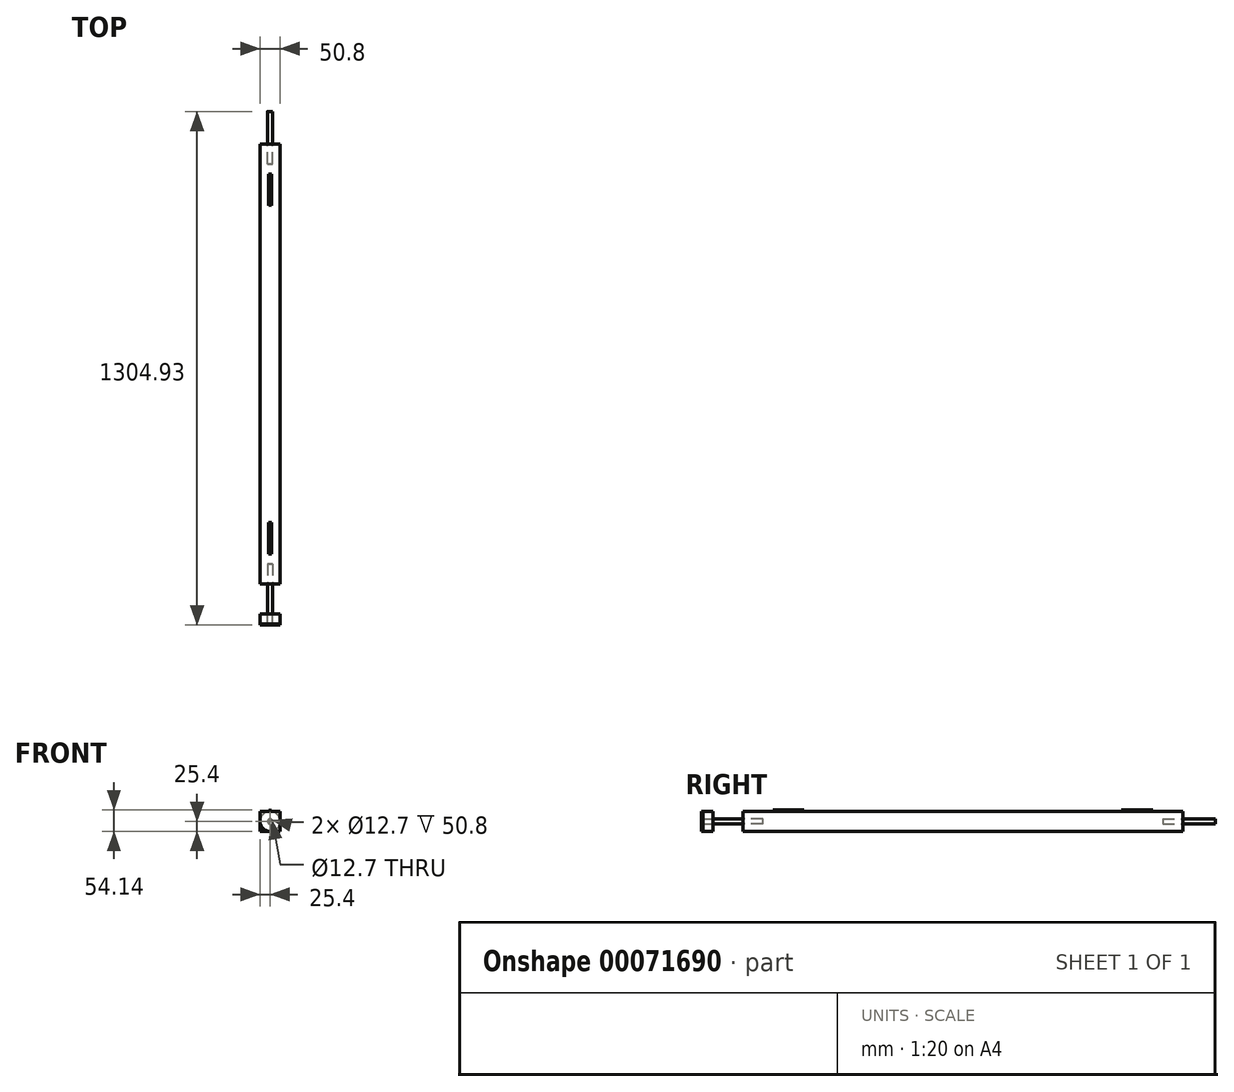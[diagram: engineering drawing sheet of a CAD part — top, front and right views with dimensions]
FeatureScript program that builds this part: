
annotation { "Feature Type Name" : "Feature", "Feature Type Description" : "" }
export const myFeature = defineFeature(function(context is Context, id is Id, definition is map)
    precondition{}
    {
        {
            var Q0;
            Q0=qCreatedBy(makeId("Front.planeOp"),FACE);
            var sketch = newSketch(context, id + "F0", { "sketchPlane" : qUnion([Q0])});
            skCircle(sketch, "E0", {"center": v(0, 0) * mm, "radius": 25.4 * mm});
            skSolve(sketch);
        }
        {
            var Q0;
            Q0=makeQuery(id+"F0.imprint","IMPRINT",FACE,{"disambiguationData":[TD([[makeQuery(id+"F0.imprint","IMPRINT",EDGE,{"derivedFrom":sQuery(id+"F0.wireOp",EDGE,"E0")}),1.0]])]});
            extrude(context, id + "F1", {"entities" : qUnion([Q0]), "depth" : 1117.6 * mm});
        }
        {
            var Q0;
            Q0=makeQuery(id+"F1.opExtrude","CAP_FACE",FACE,{"disambiguationData":[OSD([sQuery(id+"F0.wireOp",EDGE,"E0")])],"isStart":true});
            var sketch = newSketch(context, id + "F2", { "sketchPlane" : qUnion([Q0])});
            skCircle(sketch, "E1.0", {"center": v(0, 0) * mm, "radius": 25.4 * mm});
            skCircle(sketch, "E2", {"center": v(0, 0) * mm, "radius": 6.35 * mm});
            skSolve(sketch);
        }
        {
            var Q0;
            Q0=makeQuery(id+"F2.imprint","IMPRINT",FACE,{"disambiguationData":[TD([[makeQuery(id+"F2.imprint","IMPRINT",EDGE,{"derivedFrom":sQuery(id+"F2.wireOp",EDGE,"E2")}),1.0]])]});
            extrude(context, id + "F3", {"entities" : qUnion([Q0]), "operationType" : NewBodyOperationType.REMOVE, "oppositeDirection" : true, "depth" : 50.8 * mm});
        }
        {
            var Q0;
            Q0=makeQuery(id+"F1.opExtrude","CAP_FACE",FACE,{"disambiguationData":[OSD([sQuery(id+"F0.wireOp",EDGE,"E0")])],"isStart":false});
            var sketch = newSketch(context, id + "F4", { "sketchPlane" : qUnion([Q0])});
            skCircle(sketch, "E3.0", {"center": v(0, 0) * mm, "radius": 25.4 * mm});
            skCircle(sketch, "E4", {"center": v(0, 0) * mm, "radius": 6.35 * mm});
            skSolve(sketch);
        }
        {
            var Q0;
            Q0=makeQuery(id+"F4.imprint","IMPRINT",FACE,{"disambiguationData":[TD([[makeQuery(id+"F4.imprint","IMPRINT",EDGE,{"derivedFrom":sQuery(id+"F4.wireOp",EDGE,"E4")}),1.0]])]});
            extrude(context, id + "F5", {"entities" : qUnion([Q0]), "operationType" : NewBodyOperationType.REMOVE, "oppositeDirection" : true, "depth" : 50.8 * mm});
        }
        {
            var Q0;
            Q0=makeQuery(id+"F4.imprint","IMPRINT",FACE,{"disambiguationData":[TD([[makeQuery(id+"F4.imprint","IMPRINT",EDGE,{"derivedFrom":sQuery(id+"F4.wireOp",EDGE,"E4")}),1.0]])]});
            extrude(context, id + "F6", {"entities" : qUnion([Q0]), "depth" : 76.2 * mm});
        }
        {
            var Q0;
            Q0=makeQuery(id+"F6.opExtrude","CAP_FACE",FACE,{"disambiguationData":[OSD([sQuery(id+"F4.wireOp",EDGE,"E4")])],"isStart":false});
            var sketch = newSketch(context, id + "F7", { "sketchPlane" : qUnion([Q0])});
            skCircle(sketch, "E5.0", {"center": v(0, 0) * mm, "radius": 25.4 * mm});
            skCircle(sketch, "E5.1", {"center": v(0, 0) * mm, "radius": 6.35 * mm});
            skSolve(sketch);
        }
        {
            var Q0;
            Q0=makeQuery(id+"F7.imprint","IMPRINT",FACE,{"disambiguationData":[TD([[makeQuery(id+"F7.imprint","IMPRINT",EDGE,{"derivedFrom":sQuery(id+"F7.wireOp",EDGE,"E5.0")}),1.0]])]});
            extrude(context, id + "F8", {"entities" : qUnion([Q0]), "depth" : 25.4 * mm});
        }
        {
            var Q0;
            Q0=makeQuery(id+"F2.imprint","IMPRINT",FACE,{"disambiguationData":[TD([[makeQuery(id+"F2.imprint","IMPRINT",EDGE,{"derivedFrom":sQuery(id+"F2.wireOp",EDGE,"E2")}),1.0]])]});
            extrude(context, id + "F9", {"entities" : qUnion([Q0]), "depth" : 82.55 * mm});
        }
        {
            var Q0;
            Q0=makeQuery(id+"F8.opExtrude","CAP_FACE",FACE,{"disambiguationData":[OSD([sQuery(id+"F7.wireOp",EDGE,"E5.0"),sQuery(id+"F7.wireOp",EDGE,"E5.1")])],"isStart":false});
            var sketch = newSketch(context, id + "F10", { "sketchPlane" : qUnion([Q0])});
            skLineSegment(sketch, "E6.rect.bottom", {"start": v(-25.4, 25.4) * mm, "end": v(25.4, 25.4) * mm});
            skLineSegment(sketch, "E6.rect.top", {"start": v(-25.4, -25.4) * mm, "end": v(25.4, -25.4) * mm});
            skLineSegment(sketch, "E6.rect.left", {"start": v(-25.4, 25.4) * mm, "end": v(-25.4, -25.4) * mm});
            skLineSegment(sketch, "E6.rect.right", {"start": v(25.4, 25.4) * mm, "end": v(25.4, -25.4) * mm});
            skPoint(sketch, "E6.rect.middle", {"position": v(0, 0) * mm});
            skSolve(sketch);
        }
        {
            var Q0;
            Q0=makeQuery(id+"F10.imprint","IMPRINT",FACE,{"disambiguationData":[TD([[makeQuery(id+"F10.imprint","IMPRINT",EDGE,{"derivedFrom":sQuery(id+"F10.wireOp",EDGE,"E6.rect.bottom")}),-1.0]])]});
            var Q1;
            Q1=makeQuery(id+"F10.imprint","IMPRINT",FACE,{"disambiguationData":[TD([[makeQuery(id+"F10.imprint","IMPRINT",EDGE,{"derivedFrom":makeQuery(id+"F8.opExtrude","CAP_EDGE",EDGE,{"disambiguationData":[OSD([sQuery(id+"F7.wireOp",EDGE,"E5.0")])],"isStart":false})}),1.0]])]});
            var Q2;
            Q2=makeQuery(id+"F10.imprint","IMPRINT",FACE,{"disambiguationData":[TD([[makeQuery(id+"F10.imprint","IMPRINT",EDGE,{"derivedFrom":makeQuery(id+"F8.opExtrude","CAP_EDGE",EDGE,{"disambiguationData":[OSD([sQuery(id+"F7.wireOp",EDGE,"E5.1")])],"isStart":false})}),1.0]])]});
            var Q3;
            {var subQ0=sQuery(id+"F10.wireOp",EDGE,"E6.rect.left");var subQ1=sQuery(id+"F10.wireOp",EDGE,"E6.rect.top");var subQ2=makeQuery(id+"F10.imprint","INTERSECT",VERTEX,{"derivedFrom":[subQ1,subQ0]});Q3=makeQuery(id+"F10.imprint","IMPRINT",FACE,{"disambiguationData":[TD([[makeQuery(id+"F10.imprint","IMPRINT",EDGE,{"disambiguationData":[TD([[subQ2,-1.0]])],"derivedFrom":subQ1}),1.0]])]});}
            var Q4;
            {var subQ0=sQuery(id+"F10.wireOp",EDGE,"E6.rect.right");var subQ1=sQuery(id+"F10.wireOp",EDGE,"E6.rect.top");var subQ2=makeQuery(id+"F10.imprint","INTERSECT",VERTEX,{"derivedFrom":[subQ1,subQ0]});Q4=makeQuery(id+"F10.imprint","IMPRINT",FACE,{"disambiguationData":[TD([[makeQuery(id+"F10.imprint","IMPRINT",EDGE,{"disambiguationData":[TD([[subQ2,1.0]])],"derivedFrom":subQ1}),1.0]])]});}
            extrude(context, id + "F11", {"entities" : qUnion([Q0, Q1, Q2, Q3, Q4]), "depth" : 3.17 * mm});
        }
        {
            var Q0;
            Q0=qCreatedBy(makeId("Right.planeOp"),FACE);
            var sketch = newSketch(context, id + "F12", { "sketchPlane" : qUnion([Q0])});
            skLineSegment(sketch, "E7.0", {"start": v(0, 25.4) * mm, "end": v(0, -25.4) * mm});
            skLineSegment(sketch, "E8.0", {"start": v(-1117.6, -25.4) * mm, "end": v(-1117.6, 25.4) * mm});
            skLineSegment(sketch, "E9", {"start": v(0, 25.4) * mm, "end": v(-1117.6, 25.4) * mm});
            skLineSegment(sketch, "E10", {"start": v(-1117.6, -25.4) * mm, "end": v(0, -25.4) * mm});
            skLineSegment(sketch, "E11", {"start": v(-558.8, 25.4) * mm, "end": v(-558.8, -25.4) * mm, "construction": true});
            skLineSegment(sketch, "E12", {"start": v(-77.79, 25.4) * mm, "end": v(-77.79, 26.99) * mm});
            skLineSegment(sketch, "E13", {"start": v(-77.79, 26.99) * mm, "end": v(-153.99, 26.99) * mm});
            skLineSegment(sketch, "E14", {"start": v(-153.99, 26.99) * mm, "end": v(-153.99, 25.4) * mm});
            skLineSegment(sketch, "E15.0", {"start": v(-155.58, 28.58) * mm, "end": v(-155.58, 25.4) * mm});
            skLineSegment(sketch, "E15.1", {"start": v(-76.2, 28.58) * mm, "end": v(-155.58, 28.58) * mm});
            skLineSegment(sketch, "E15.2", {"start": v(-76.2, 25.4) * mm, "end": v(-76.2, 28.58) * mm});
            skLineSegment(sketch, "E16.MirrorCS", {"start": v(-1039.81, 25.4) * mm, "end": v(-1039.81, 26.99) * mm});
            skLineSegment(sketch, "E17.MirrorCS", {"start": v(-1041.4, 25.4) * mm, "end": v(-1041.4, 28.57) * mm});
            skLineSegment(sketch, "E18.MirrorCS", {"start": v(-1041.4, 28.57) * mm, "end": v(-962.03, 28.57) * mm});
            skLineSegment(sketch, "E19.MirrorCS", {"start": v(-1039.81, 26.99) * mm, "end": v(-963.61, 26.99) * mm});
            skLineSegment(sketch, "E20.MirrorCS", {"start": v(-962.03, 28.58) * mm, "end": v(-962.03, 25.4) * mm});
            skLineSegment(sketch, "E21.MirrorCS", {"start": v(-963.61, 26.99) * mm, "end": v(-963.61, 25.4) * mm});
            skSolve(sketch);
        }
        {
            var Q0;
            {var subQ0=sQuery(id+"F12.wireOp",EDGE,"E12");Q0=makeQuery(id+"F12.imprint","IMPRINT",FACE,{"disambiguationData":[TD([[makeQuery(id+"F12.imprint","IMPRINT",EDGE,{"derivedFrom":subQ0}),-1.0]])]});}
            var Q1;
            {var subQ1=sQuery(id+"F12.wireOp",EDGE,"E16.MirrorCS");Q1=makeQuery(id+"F12.imprint","IMPRINT",FACE,{"disambiguationData":[TD([[makeQuery(id+"F12.imprint","IMPRINT",EDGE,{"derivedFrom":subQ1}),1.0]])]});}
            extrude(context, id + "F13", {"entities" : qUnion([Q0, Q1]), "operationType" : NewBodyOperationType.ADD, "endBound" : BoundingType.SYMMETRIC, "depth" : 6.35 * mm, "hasDraft" : true, "draftAngle" : 3 * degree});
        }
    });
